# Revit family: Haworth_BeHold_Modular_AttachedCredenza_StorageEnd
name_source: partatom
category: Furniture Systems
revit_build: Autodesk Revit 2018 (Build: 20170223_1515(x64)
units: mm (PartAtom-declared; Revit-internal decimal feet)

## family parameters
Always vertical = Yes
Cut with Voids When Loaded = No
OmniClass Number = 23.40.70.14.64.21
OmniClass Title = Systems Furniture
Part Type = Normal
Room Calculation Point = No
Round Connector Dimension = Use Diameter
Shared = No
Work Plane-Based = No

## types (8) — shared parameters
16 Deep Leg = No
Actual D/T Leg Control = No
Actual Depth = 24"
Assembly Code = E2020200
Blade Pull = Yes
Case Thickness = 3/4"
Classic Pull = No
Classic Pull Length = 6 3/4"
Cresent Pull = No
Custom Size = No
Depth = 24"
Description = Haworth - Be_Hold - Credenza
Double Unit Leg = No
Glide Finish = Haworth _ Polymer _ Slate
Leg Height = 6"
Linear Pull = No
Linear Pull Length = 8"
Manufacturer = Haworth
Max. Depth = 24"
Max. Height = 42"
Max. Storage Width = 42"
Max. Width = 72"
Min. Depth = 16"
Min. Height = 22"
Model = Haworth Be_Hold
Revision Number = 1
Shelf 1 Offset = 13 5/16"
Single Unit Leg = Yes
Size = Verify Final Dim. w/ Haworth
Standard Depths = 16, 24 in.
Sustainability Info = https://www.haworth.com
Top Thickness = 3/4"
Triple Unit Leg = No
URL = www.haworth.com
URL - Product = http://www.haworth.com
Warranty = http://www.haworth.com
Wing Pull = No
Wing Pull Length = 16 3/4"
With Lock = Yes

## per-type parameters (varying)
- 2H - 72w - 42w Drawer - Proud Back: Actual Height=28"; Actual Single Leg Control=No; Actual Storage Width=42"; Actual Width=72"; Back Case Back Control=0"; Back Case Side Control=0"; Back Door Height=26 3/16"; Blade Pull Length=41 13/16"; Bottom Case Offset=1/2"; Bottom Drawer Control=Yes; Bottom Drawer Height=13 1/8"; Bottom Drawer Offset=1 3/8"; Box Box File=Yes; Box File=No; Distance Between Drawer=1/4"; Door Width=34 1/2"; Drawer Width=41 7/8"; Drawers=Yes; File File=No; Front Door Height=26 3/8"; Glide Control=Yes; Inset Style=No; Mid Separator O/D Control=Yes; Mid Separator S/D Control=No; Middle Drawer Control=Yes; Middle Drawer Height=6 9/16"; Min. Storage Width=24"; Min. Width=42"; One and One Half High=No; Open=No; Proud Style=Yes; Separator Case Front Offset=3/4"; Shelf 2 Offset=13 5/16"; Shelf Bottom Control=No; Shelf Front Offset=3/4"; Shelf Top Control=No; Side Case Back Control=3/4"; Side Case Front Control=3/4"; Sliding Door=No; Sliding Door Control=No; Standard Height=1.5, 2 High; Standard Storage Height=28"; Standard Widths=42-72 in. @ 6 in. increments; Storage Width=42"; Three High=No; Top Case Back Control=0"; Top Case Front Offset=3"; Top Drawer Control=Yes; Top Drawer Height=6 9/16"; Total Drawer Height=26 1/2"; Two High=Yes; Width=72"; With Leg=No
- 1.5H - 60w - 36w Drawer - Inset Back: Actual Height=22"; Actual Single Leg Control=No; Actual Storage Width=36"; Actual Width=60"; Back Case Back Control=3/16"; Back Case Side Control=3/4"; Back Door Height=20 3/16"; Blade Pull Length=35 13/16"; Bottom Case Offset=1/2"; Bottom Drawer Control=Yes; Bottom Drawer Height=13 149/256"; Bottom Drawer Offset=1 3/8"; Box Box File=No; Box File=Yes; Distance Between Drawer=1/8"; Door Width=28 1/2"; Drawer Width=35 7/8"; Drawers=Yes; File File=No; Front Door Height=20 3/8"; Glide Control=Yes; Inset Style=Yes; Mid Separator O/D Control=Yes; Mid Separator S/D Control=No; Middle Drawer Control=No; Middle Drawer Height=6 203/256"; Min. Storage Width=24"; Min. Width=42"; One and One Half High=Yes; Open=No; Proud Style=No; Separator Case Front Offset=3/4"; Shelf 2 Offset=13 5/16"; Shelf Bottom Control=No; Shelf Front Offset=3/4"; Shelf Top Control=No; Side Case Back Control=0"; Side Case Front Control=3/4"; Sliding Door=No; Sliding Door Control=No; Standard Height=1.5, 2 High; Standard Storage Height=22"; Standard Widths=42-72 in. @ 6 in. increments; Storage Width=36"; Three High=No; Top Case Back Control=3/16"; Top Case Front Offset=3"; Top Drawer Control=Yes; Top Drawer Height=6 203/256"; Total Drawer Height=20 1/2"; Two High=No; Width=60"; With Leg=No
- 2H - 72w - 36w Open - Proud Back: Actual Height=28"; Actual Single Leg Control=No; Actual Storage Width=36"; Actual Width=72"; Back Case Back Control=0"; Back Case Side Control=0"; Back Door Height=26 3/16"; Blade Pull Length=35 13/16"; Bottom Case Offset=1/2"; Bottom Drawer Control=No; Bottom Drawer Height=13 3/16"; Bottom Drawer Offset=1 3/8"; Box Box File=No; Box File=No; Distance Between Drawer=1/8"; Door Width=34 1/2"; Drawer Width=35 7/8"; Drawers=No; File File=Yes; Front Door Height=26 3/8"; Glide Control=Yes; Inset Style=No; Mid Separator O/D Control=Yes; Mid Separator S/D Control=No; Middle Drawer Control=No; Middle Drawer Height=13 3/16"; Min. Storage Width=24"; Min. Width=42"; One and One Half High=No; Open=Yes; Proud Style=Yes; Separator Case Front Offset=0"; Shelf 2 Offset=13 5/16"; Shelf Bottom Control=Yes; Shelf Front Offset=3/4"; Shelf Top Control=No; Side Case Back Control=3/4"; Side Case Front Control=0"; Sliding Door=No; Sliding Door Control=No; Standard Height=1.5, 2 High; Standard Storage Height=28"; Standard Widths=42-72 in. @ 6 in. increments; Storage Width=36"; Three High=No; Top Case Back Control=0"; Top Case Front Offset=3"; Top Drawer Control=No; Top Drawer Height=13 3/16"; Total Drawer Height=26 1/2"; Two High=Yes; Width=72"; With Leg=No
- 1.5H - 60w - 30w Open - Inset Back: Actual Height=22"; Actual Single Leg Control=No; Actual Storage Width=30"; Actual Width=60"; Back Case Back Control=3/16"; Back Case Side Control=3/4"; Back Door Height=20 3/16"; Blade Pull Length=29 13/16"; Bottom Case Offset=1/2"; Bottom Drawer Control=No; Bottom Drawer Height=13 149/256"; Bottom Drawer Offset=1 3/8"; Box Box File=No; Box File=No; Distance Between Drawer=1/8"; Door Width=28 1/2"; Drawer Width=29 7/8"; Drawers=No; File File=Yes; Front Door Height=20 3/8"; Glide Control=Yes; Inset Style=Yes; Mid Separator O/D Control=Yes; Mid Separator S/D Control=No; Middle Drawer Control=No; Middle Drawer Height=10 3/16"; Min. Storage Width=24"; Min. Width=42"; One and One Half High=Yes; Open=Yes; Proud Style=No; Separator Case Front Offset=0"; Shelf 2 Offset=13 5/16"; Shelf Bottom Control=Yes; Shelf Front Offset=3/4"; Shelf Top Control=No; Side Case Back Control=0"; Side Case Front Control=0"; Sliding Door=No; Sliding Door Control=No; Standard Height=1.5, 2 High; Standard Storage Height=22"; Standard Widths=42-72 in. @ 6 in. increments; Storage Width=30"; Three High=No; Top Case Back Control=3/16"; Top Case Front Offset=3"; Top Drawer Control=No; Top Drawer Height=13 149/256"; Total Drawer Height=20 1/2"; Two High=No; Width=60"; With Leg=No
- 1.5H - 48w - 24w Door - Inset Back: Actual Height=22"; Actual Single Leg Control=No; Actual Storage Width=24"; Actual Width=48"; Back Case Back Control=3/16"; Back Case Side Control=3/4"; Back Door Height=20 3/16"; Blade Pull Length=23 13/16"; Bottom Case Offset=1/2"; Bottom Drawer Control=No; Bottom Drawer Height=13 149/256"; Bottom Drawer Offset=1 3/8"; Box Box File=No; Box File=No; Distance Between Drawer=1/8"; Door Width=22 1/2"; Drawer Width=23 7/8"; Drawers=No; File File=Yes; Front Door Height=20 3/8"; Glide Control=Yes; Inset Style=Yes; Mid Separator O/D Control=No; Mid Separator S/D Control=Yes; Middle Drawer Control=No; Middle Drawer Height=10 3/16"; Min. Storage Width=18"; Min. Width=36"; One and One Half High=Yes; Open=No; Proud Style=No; Separator Case Front Offset=3/4"; Shelf 2 Offset=13 5/16"; Shelf Bottom Control=Yes; Shelf Front Offset=2 1/8"; Shelf Top Control=No; Side Case Back Control=0"; Side Case Front Control=0"; Sliding Door=Yes; Sliding Door Control=Yes; Standard Height=1.5, 2, 3 High; Standard Storage Height=22"; Standard Widths=36-72 in. @ 6 in. increments; Storage Width=24"; Three High=No; Top Case Back Control=3/16"; Top Case Front Offset=2 1/8"; Top Drawer Control=No; Top Drawer Height=13 149/256"; Total Drawer Height=20 1/2"; Two High=No; Width=48"; With Leg=No
- 2H - 60w - 30w Door - Proud Back: Actual Height=28"; Actual Single Leg Control=No; Actual Storage Width=30"; Actual Width=60"; Back Case Back Control=0"; Back Case Side Control=0"; Back Door Height=26 3/16"; Blade Pull Length=29 13/16"; Bottom Case Offset=1/2"; Bottom Drawer Control=No; Bottom Drawer Height=13 3/16"; Bottom Drawer Offset=1 3/8"; Box Box File=No; Box File=No; Distance Between Drawer=1/8"; Door Width=28 1/2"; Drawer Width=29 7/8"; Drawers=No; File File=Yes; Front Door Height=26 3/8"; Glide Control=Yes; Inset Style=No; Mid Separator O/D Control=No; Mid Separator S/D Control=Yes; Middle Drawer Control=No; Middle Drawer Height=13 3/16"; Min. Storage Width=18"; Min. Width=36"; One and One Half High=No; Open=No; Proud Style=Yes; Separator Case Front Offset=3/4"; Shelf 2 Offset=13 5/16"; Shelf Bottom Control=Yes; Shelf Front Offset=2 1/8"; Shelf Top Control=No; Side Case Back Control=3/4"; Side Case Front Control=0"; Sliding Door=Yes; Sliding Door Control=Yes; Standard Height=1.5, 2, 3 High; Standard Storage Height=28"; Standard Widths=36-72 in. @ 6 in. increments; Storage Width=30"; Three High=No; Top Case Back Control=0"; Top Case Front Offset=2 1/8"; Top Drawer Control=No; Top Drawer Height=13 3/16"; Total Drawer Height=26 1/2"; Two High=Yes; Width=60"; With Leg=No
- 3H - 72w - 36w Door - Inset Back: Actual Height=42"; Actual Single Leg Control=No; Actual Storage Width=36"; Actual Width=72"; Back Case Back Control=3/16"; Back Case Side Control=3/4"; Back Door Height=40 3/16"; Blade Pull Length=35 13/16"; Bottom Case Offset=1/2"; Bottom Drawer Control=No; Bottom Drawer Height=13 117/256"; Bottom Drawer Offset=1 3/8"; Box Box File=No; Box File=No; Distance Between Drawer=1/8"; Door Width=34 1/2"; Drawer Width=35 7/8"; Drawers=No; File File=Yes; Front Door Height=40 3/8"; Glide Control=Yes; Inset Style=Yes; Mid Separator O/D Control=No; Mid Separator S/D Control=Yes; Middle Drawer Control=No; Middle Drawer Height=20 3/16"; Min. Storage Width=18"; Min. Width=36"; One and One Half High=No; Open=No; Proud Style=No; Separator Case Front Offset=3/4"; Shelf 2 Offset=26 5/8"; Shelf Bottom Control=Yes; Shelf Front Offset=2 1/8"; Shelf Top Control=Yes; Side Case Back Control=0"; Side Case Front Control=0"; Sliding Door=Yes; Sliding Door Control=Yes; Standard Height=1.5, 2, 3 High; Standard Storage Height=42"; Standard Widths=36-72 in. @ 6 in. increments; Storage Width=36"; Three High=Yes; Top Case Back Control=3/16"; Top Case Front Offset=2 1/8"; Top Drawer Control=No; Top Drawer Height=13 117/256"; Total Drawer Height=40 1/2"; Two High=No; Width=72"; With Leg=No
- 1.5H - 60w - 36w Drawer - Inset Back - With Leg: Actual Height=28"; Actual Single Leg Control=Yes; Actual Storage Width=36"; Actual Width=60"; Back Case Back Control=3/16"; Back Case Side Control=3/4"; Back Door Height=20 11/16"; Blade Pull Length=35 13/16"; Bottom Case Offset=6"; Bottom Drawer Control=Yes; Bottom Drawer Height=13 235/256"; Bottom Drawer Offset=6 7/8"; Box Box File=No; Box File=Yes; Distance Between Drawer=1/8"; Door Width=28 1/2"; Drawer Width=35 7/8"; Drawers=Yes; File File=No; Front Door Height=20 7/8"; Glide Control=No; Inset Style=Yes; Mid Separator O/D Control=Yes; Mid Separator S/D Control=No; Middle Drawer Control=No; Middle Drawer Height=6 245/256"; Min. Storage Width=24"; Min. Width=42"; One and One Half High=Yes; Open=No; Proud Style=No; Separator Case Front Offset=3/4"; Shelf 2 Offset=13 5/16"; Shelf Bottom Control=No; Shelf Front Offset=3/4"; Shelf Top Control=No; Side Case Back Control=0"; Side Case Front Control=3/4"; Sliding Door=No; Sliding Door Control=No; Standard Height=1.5, 2 High; Standard Storage Height=22"; Standard Widths=42-72 in. @ 6 in. increments; Storage Width=36"; Three High=No; Top Case Back Control=3/16"; Top Case Front Offset=3"; Top Drawer Control=Yes; Top Drawer Height=6 245/256"; Total Drawer Height=21"; Two High=No; Width=60"; With Leg=Yes

## geometry (parser evidence)
native form markers: Sweep x14
no freeform markers — native parametric forms only
